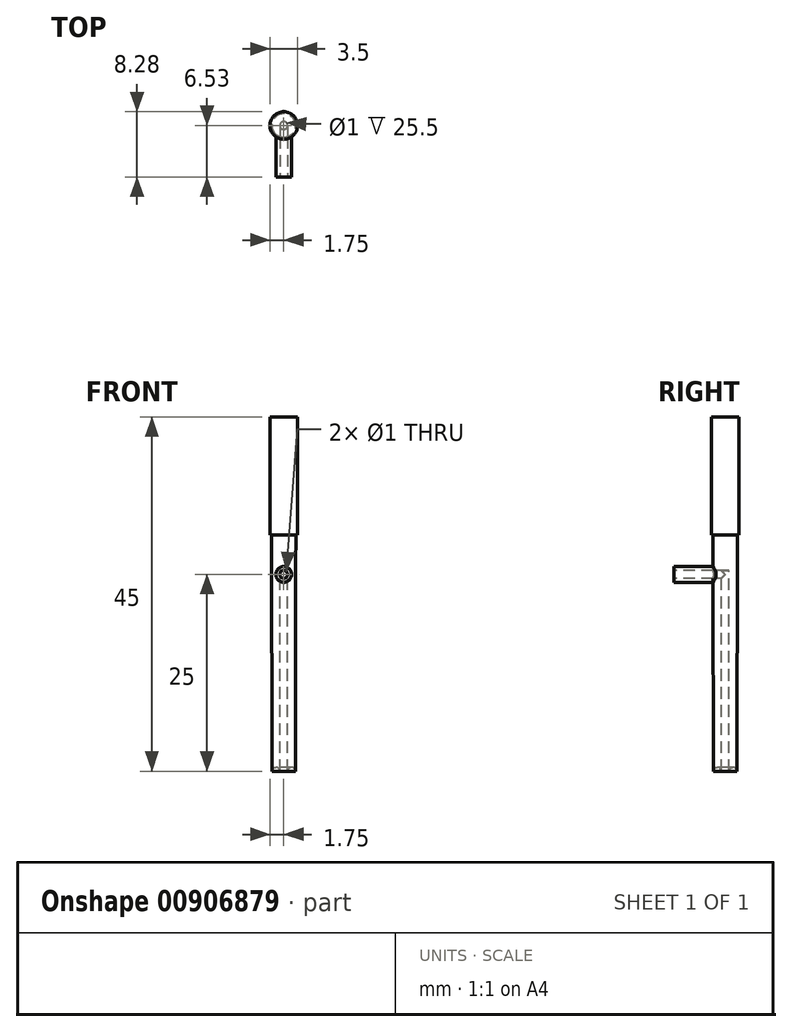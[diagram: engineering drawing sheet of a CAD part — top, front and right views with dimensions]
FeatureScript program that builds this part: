
annotation { "Feature Type Name" : "Feature", "Feature Type Description" : "" }
export const myFeature = defineFeature(function(context is Context, id is Id, definition is map)
    precondition{}
    {
        {
            var Q0;
            Q0=qCreatedBy(makeId("Front.planeOp"),FACE);
            var sketch = newSketch(context, id + "F0", { "sketchPlane" : qUnion([Q0])});
            skLineSegment(sketch, "E0.right", {"start": v(-1.5, -15) * mm, "end": v(-1.53, 15) * mm});
            skPoint(sketch, "E0.middle", {"position": v(0, 0) * mm});
            skPoint(sketch, "E1.middle", {"position": v(0, 22.5) * mm});
            skLineSegment(sketch, "E2", {"start": v(0, 30) * mm, "end": v(0, -15) * mm});
            skLineSegment(sketch, "E3.top", {"start": v(0, 10.5) * mm, "end": v(-0.5, 10.5) * mm});
            skLineSegment(sketch, "E3.right", {"start": v(-0.5, -15) * mm, "end": v(-0.5, 10.5) * mm});
            skArc(sketch, "E4", {"start": v(-0.5, -15) * mm, "mid": v(-1, -14.5) * mm, "end": v(-1.5, -15) * mm});
            skLineSegment(sketch, "E5", {"start": v(0, 30) * mm, "end": v(-1.75, 30) * mm});
            skLineSegment(sketch, "E6", {"start": v(-1.75, 30) * mm, "end": v(-1.75, 15) * mm});
            skLineSegment(sketch, "E7", {"start": v(-1.75, 15) * mm, "end": v(-1.53, 15) * mm});
            skSolve(sketch);
        }
        {
            var Q0;
            Q0 = qSketchRegion(id + "F0", true);
            var Q1;
            Q1=sQuery(id+"F0.wireOp",EDGE,"E2");
            revolve(context, id + "F1", {"surfaceOperationType" : NewSurfaceOperationType.NEW, "entities" : qUnion([Q0]), "axis" : qUnion([Q1]), "revolveType" : RevolveType.FULL});
        }
        {
            var Q0;
            Q0=qCreatedBy(makeId("Top.planeOp"),FACE);
            var sketch = newSketch(context, id + "F2", { "sketchPlane" : qUnion([Q0])});
            skLineSegment(sketch, "E8", {"start": v(0, 0) * mm, "end": v(0, -1.53) * mm});
            skSolve(sketch);
        }
        {
            var Q0;
            Q0=qCreatedBy(makeId("Front.planeOp"),FACE);
            var Q1;
            Q1=sQuery(id+"F2.wireOp",VERTEX,"E8.end");
            cPlane(context, id + "F3", {"entities" : qUnion([Q0, Q1]), "cplaneType" : CPlaneType.PLANE_POINT, "offset" : 25 * mm, "width" : 150 * mm, "height" : 150 * mm});
        }
        {
            var Q0;
            Q0=qCreatedBy(id+"F3.planeOp",FACE);
            var sketch = newSketch(context, id + "F4", { "sketchPlane" : qUnion([Q0])});
            skCircle(sketch, "E9", {"center": v(0, 10) * mm, "radius": 0.5 * mm});
            skCircle(sketch, "E10", {"center": v(0, 10) * mm, "radius": 1 * mm});
            skSolve(sketch);
        }
        {
            var Q0;
            Q0=makeQuery(id+"F4.imprint","IMPRINT",FACE,{"disambiguationData":[TD([[makeQuery(id+"F4.imprint","IMPRINT",EDGE,{"derivedFrom":sQuery(id+"F4.wireOp",EDGE,"E9")}),1.0]])]});
            var Q1;
            Q1=sQuery(id+"F4.wireOp",EDGE,"E9");
            var Q2;
            Q2=makeQuery(id+"F1.opRevolve","SWEPT_FACE",FACE,{"disambiguationData":[OSD([sQuery(id+"F0.wireOp",EDGE,"E3.right")])]});
            extrude(context, id + "F5", {"entities" : qUnion([Q0]), "operationType" : NewBodyOperationType.REMOVE, "surfaceEntities" : qUnion([Q1]), "endBound" : BoundingType.UP_TO_SURFACE, "oppositeDirection" : true, "depth" : 25 * mm, "endBoundEntityFace" : qUnion([Q2]), "offsetDistance" : 25 * mm});
        }
        {
            var Q0;
            Q0=makeQuery(id+"F4.imprint","IMPRINT",FACE,{"disambiguationData":[TD([[makeQuery(id+"F4.imprint","IMPRINT",EDGE,{"derivedFrom":sQuery(id+"F4.wireOp",EDGE,"E9")}),-1.0]])]});
            var Q1;
            Q1=makeQuery(id+"F1.opRevolve","SWEPT_FACE",FACE,{"disambiguationData":[OSD([sQuery(id+"F0.wireOp",EDGE,"E0.right")])]});
            extrude(context, id + "F6", {"entities" : qUnion([Q0]), "endBound" : BoundingType.UP_TO_SURFACE, "oppositeDirection" : true, "depth" : 25 * mm, "endBoundEntityFace" : qUnion([Q1]), "offsetDistance" : 25 * mm});
        }
        {
            var Q0;
            Q0=makeQuery(id+"F4.imprint","IMPRINT",FACE,{"disambiguationData":[TD([[makeQuery(id+"F4.imprint","IMPRINT",EDGE,{"derivedFrom":sQuery(id+"F4.wireOp",EDGE,"E9")}),-1.0]])]});
            var Q1;
            Q1=sQuery(id+"F4.wireOp",EDGE,"E10");
            extrude(context, id + "F7", {"entities" : qUnion([Q0]), "operationType" : NewBodyOperationType.ADD, "surfaceEntities" : qUnion([Q1]), "depth" : 5 * mm, "offsetDistance" : 25 * mm});
        }
    });
